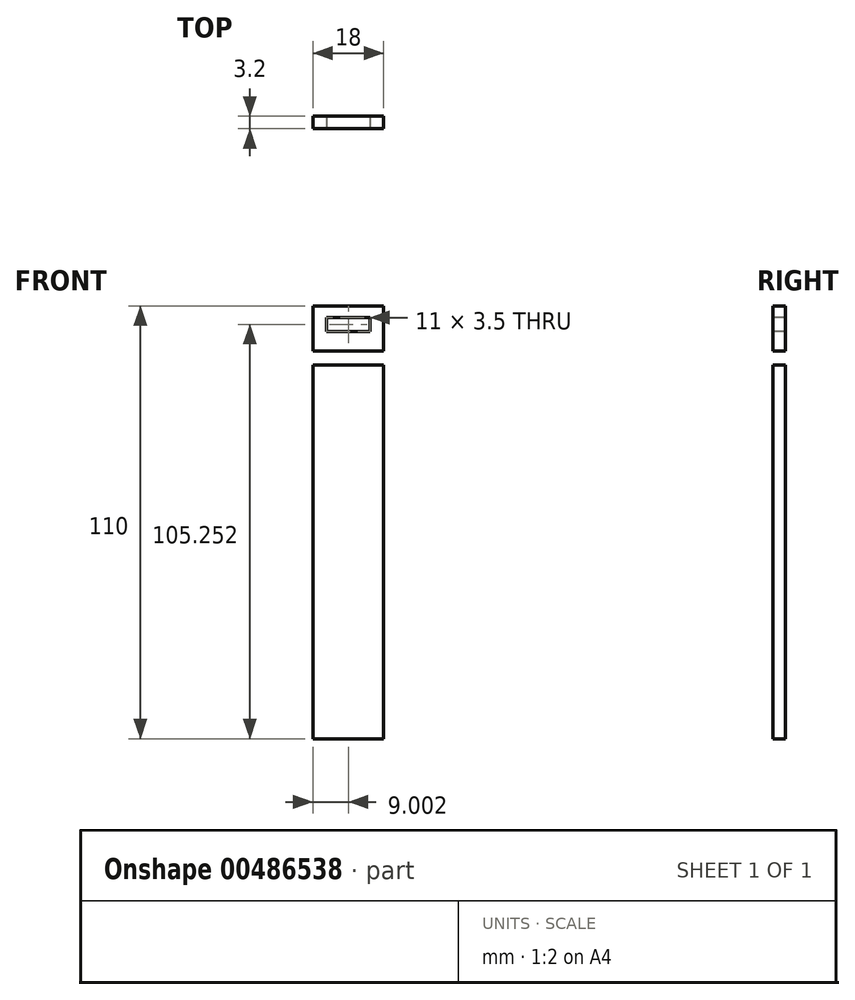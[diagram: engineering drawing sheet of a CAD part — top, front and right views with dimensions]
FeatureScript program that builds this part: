
annotation { "Feature Type Name" : "Feature", "Feature Type Description" : "" }
export const myFeature = defineFeature(function(context is Context, id is Id, definition is map)
    precondition{}
    {
        {
            var Q0;
            Q0=qCreatedBy(makeId("Front.planeOp"),FACE);
            var sketch = newSketch(context, id + "F0", { "sketchPlane" : qUnion([Q0])});
            skLineSegment(sketch, "E0.bottom", {"start": v(-5.69, 101.11) * mm, "end": v(12.31, 101.11) * mm});
            skLineSegment(sketch, "E0.top", {"start": v(-5.69, -8.89) * mm, "end": v(12.31, -8.89) * mm});
            skLineSegment(sketch, "E0.left", {"start": v(-5.69, 101.11) * mm, "end": v(-5.69, -8.89) * mm});
            skLineSegment(sketch, "E0.right", {"start": v(12.31, 101.11) * mm, "end": v(12.31, -8.89) * mm});
            skLineSegment(sketch, "E1.bottom", {"start": v(-5.69, 86.11) * mm, "end": v(12.31, 86.11) * mm});
            skLineSegment(sketch, "E1.top", {"start": v(-5.69, 89.61) * mm, "end": v(12.31, 89.61) * mm});
            skLineSegment(sketch, "E1.left", {"start": v(-5.69, 86.11) * mm, "end": v(-5.69, 89.61) * mm});
            skLineSegment(sketch, "E1.right", {"start": v(12.31, 86.11) * mm, "end": v(12.31, 89.61) * mm});
            skLineSegment(sketch, "E2.bottom", {"start": v(8.81, 89.61) * mm, "end": v(-2.19, 89.61) * mm});
            skLineSegment(sketch, "E2.top", {"start": v(8.81, 86.11) * mm, "end": v(-2.19, 86.11) * mm});
            skLineSegment(sketch, "E2.left", {"start": v(8.81, 89.61) * mm, "end": v(8.81, 86.11) * mm});
            skLineSegment(sketch, "E2.right", {"start": v(-2.19, 89.61) * mm, "end": v(-2.19, 86.11) * mm});
            skLineSegment(sketch, "E3.bottom", {"start": v(8.81, 98.11) * mm, "end": v(-2.19, 98.11) * mm});
            skLineSegment(sketch, "E3.top", {"start": v(8.81, 94.61) * mm, "end": v(-2.19, 94.61) * mm});
            skLineSegment(sketch, "E3.left", {"start": v(8.81, 98.11) * mm, "end": v(8.81, 94.61) * mm});
            skLineSegment(sketch, "E3.right", {"start": v(-2.19, 98.11) * mm, "end": v(-2.19, 94.61) * mm});
            skSolve(sketch);
        }
        {
            var Q0;
            {var subQ5=sQuery(id+"F0.wireOp",EDGE,"E0.bottom");Q0=makeQuery(id+"F0.imprint","IMPRINT",FACE,{"disambiguationData":[TD([[makeQuery(id+"F0.imprint","IMPRINT",EDGE,{"derivedFrom":subQ5}),-1.0]])]});}
            var Q1;
            {var subQ1=sQuery(id+"F0.wireOp",EDGE,"E0.top");Q1=makeQuery(id+"F0.imprint","IMPRINT",FACE,{"disambiguationData":[TD([[makeQuery(id+"F0.imprint","IMPRINT",EDGE,{"derivedFrom":subQ1}),1.0]])]});}
            var Q2;
            {var subQ0=sQuery(id+"F0.wireOp",EDGE,"E1.right");Q2=makeQuery(id+"F0.imprint","IMPRINT",FACE,{"disambiguationData":[TD([[makeQuery(id+"F0.imprint","IMPRINT",EDGE,{"derivedFrom":subQ0}),1.0]])]});}
            var Q3;
            {var subQ0=sQuery(id+"F0.wireOp",EDGE,"E1.left");Q3=makeQuery(id+"F0.imprint","IMPRINT",FACE,{"disambiguationData":[TD([[makeQuery(id+"F0.imprint","IMPRINT",EDGE,{"derivedFrom":subQ0}),-1.0]])]});}
            extrude(context, id + "F1", {"entities" : qUnion([Q0, Q1, Q2, Q3]), "oppositeDirection" : true, "depth" : 3.2 * mm, "offsetDistance" : 25 * mm});
        }
    });
